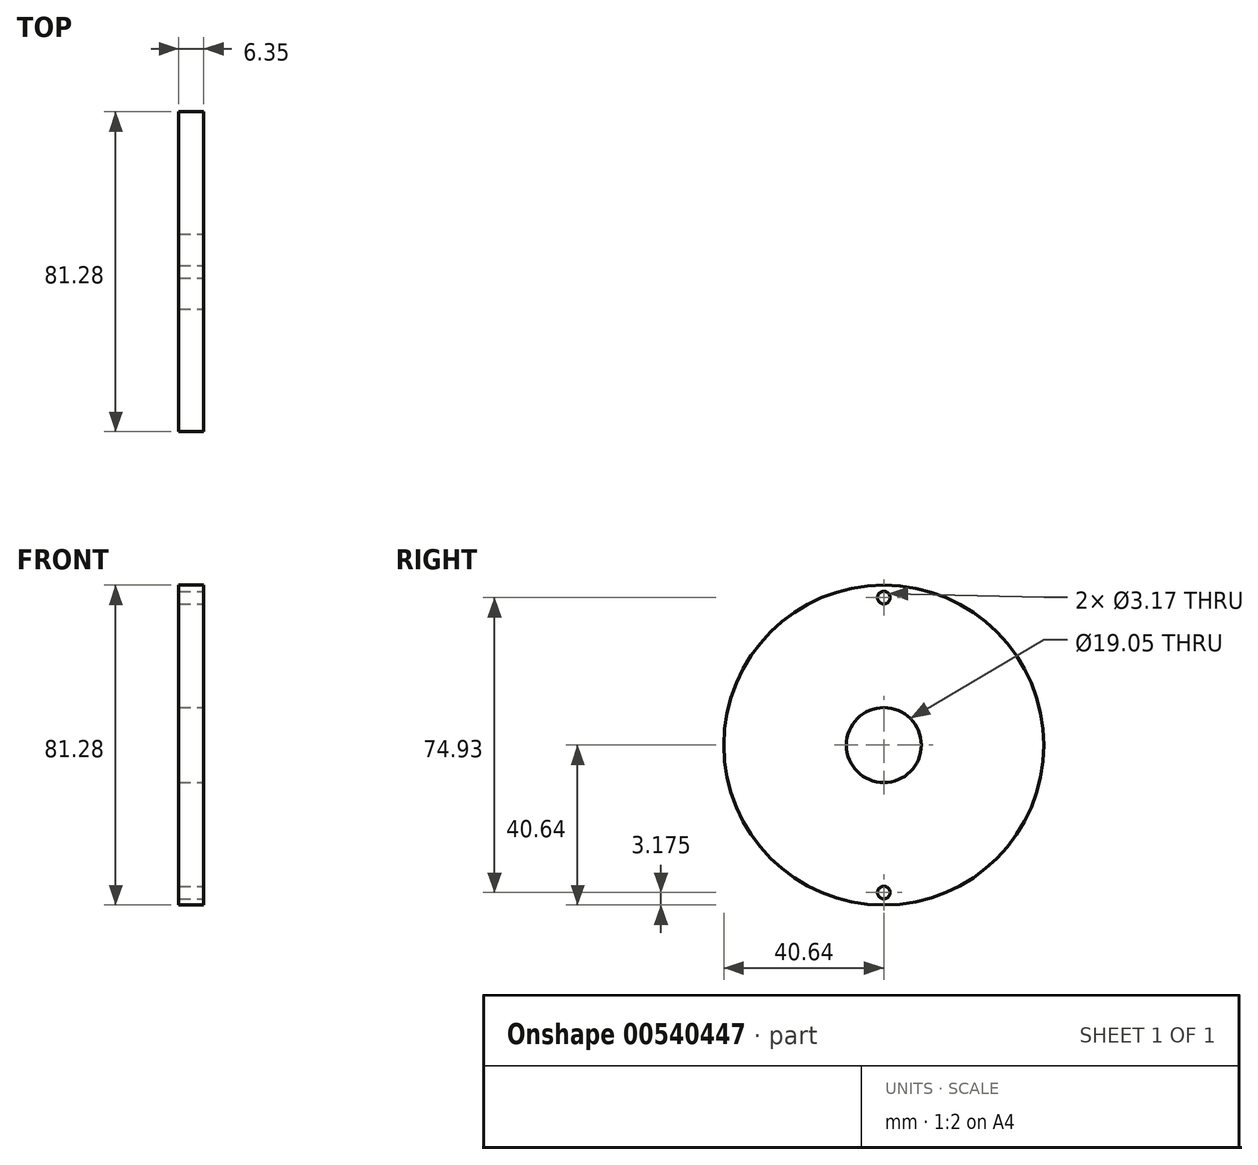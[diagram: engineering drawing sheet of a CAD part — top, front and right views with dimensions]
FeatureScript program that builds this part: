
annotation { "Feature Type Name" : "Feature", "Feature Type Description" : "" }
export const myFeature = defineFeature(function(context is Context, id is Id, definition is map)
    precondition{}
    {
        {
            var Q0;
            Q0=qCreatedBy(makeId("Right.planeOp"),FACE);
            var sketch = newSketch(context, id + "F0", { "sketchPlane" : qUnion([Q0])});
            skCircle(sketch, "E0", {"center": v(0, 0) * mm, "radius": 40.64 * mm});
            skSolve(sketch);
        }
        {
            var Q0;
            Q0 = qSketchRegion(id + "F0", true);
            extrude(context, id + "F1", {"entities" : qUnion([Q0]), "depth" : 6.35 * mm, "offsetDistance" : 25.4 * mm});
        }
        {
            var Q0;
            Q0=makeQuery(id+"F1.opExtrude","CAP_FACE",FACE,{"disambiguationData":[OSD([sQuery(id+"F0.wireOp",EDGE,"E0")])],"isStart":false});
            var sketch = newSketch(context, id + "F2", { "sketchPlane" : qUnion([Q0])});
            skCircle(sketch, "E1", {"center": v(0, 37.47) * mm, "radius": 1.59 * mm});
            skCircle(sketch, "E2", {"center": v(0, -37.47) * mm, "radius": 1.59 * mm});
            skSolve(sketch);
        }
        {
            var Q0;
            Q0 = qSketchRegion(id + "F2", true);
            extrude(context, id + "F3", {"entities" : qUnion([Q0]), "operationType" : NewBodyOperationType.REMOVE, "oppositeDirection" : true, "depth" : 6.35 * mm, "offsetDistance" : 25.4 * mm});
        }
        {
            var Q0;
            Q0=makeQuery(id+"F1.opExtrude","CAP_FACE",FACE,{"disambiguationData":[OSD([sQuery(id+"F0.wireOp",EDGE,"E0")])],"isStart":false});
            var sketch = newSketch(context, id + "F4", { "sketchPlane" : qUnion([Q0])});
            skCircle(sketch, "E3", {"center": v(0, 0) * mm, "radius": 9.53 * mm});
            skSolve(sketch);
        }
        {
            var Q0;
            Q0 = qSketchRegion(id + "F4", true);
            extrude(context, id + "F5", {"entities" : qUnion([Q0]), "operationType" : NewBodyOperationType.REMOVE, "oppositeDirection" : true, "depth" : 6.35 * mm, "offsetDistance" : 25.4 * mm});
        }
    });
